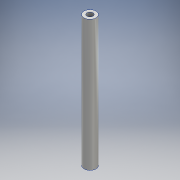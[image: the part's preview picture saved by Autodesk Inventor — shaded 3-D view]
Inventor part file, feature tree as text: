
AUTODESK INVENTOR PART (.ipt)
format: ipt  version: 2016 (Build 200138000, 138)  size: 107,008 bytes
history: native  units: mm
features: sketch x3, extrude x3, hole x2, other x1
ambient origin geometry x8: Origin, YZ Plane, XZ Plane, XY Plane, X Axis, Y Axis, Z Axis, Center Point
bodies: Body1 (feature_tree)
feature tree (9):
  other  "ソリッド1"
  sketch  "スケッチ1"
  extrude  "押し出し1"  Depth=6.0mm
  sketch  "スケッチ2"
  extrude  "押し出し2"  Depth=3.001mm
  hole  "穴1"  [1 undecoded]
  sketch  "スケッチ3"
  extrude  "押し出し3"  Depth=3.0mm
  hole  "穴2"  [1 undecoded]
note: 2 required parameter values undecoded (feature->parameter linkage not recoverable at this tier; creation-order binding heuristic only, values carry confidence <= 0.55)
